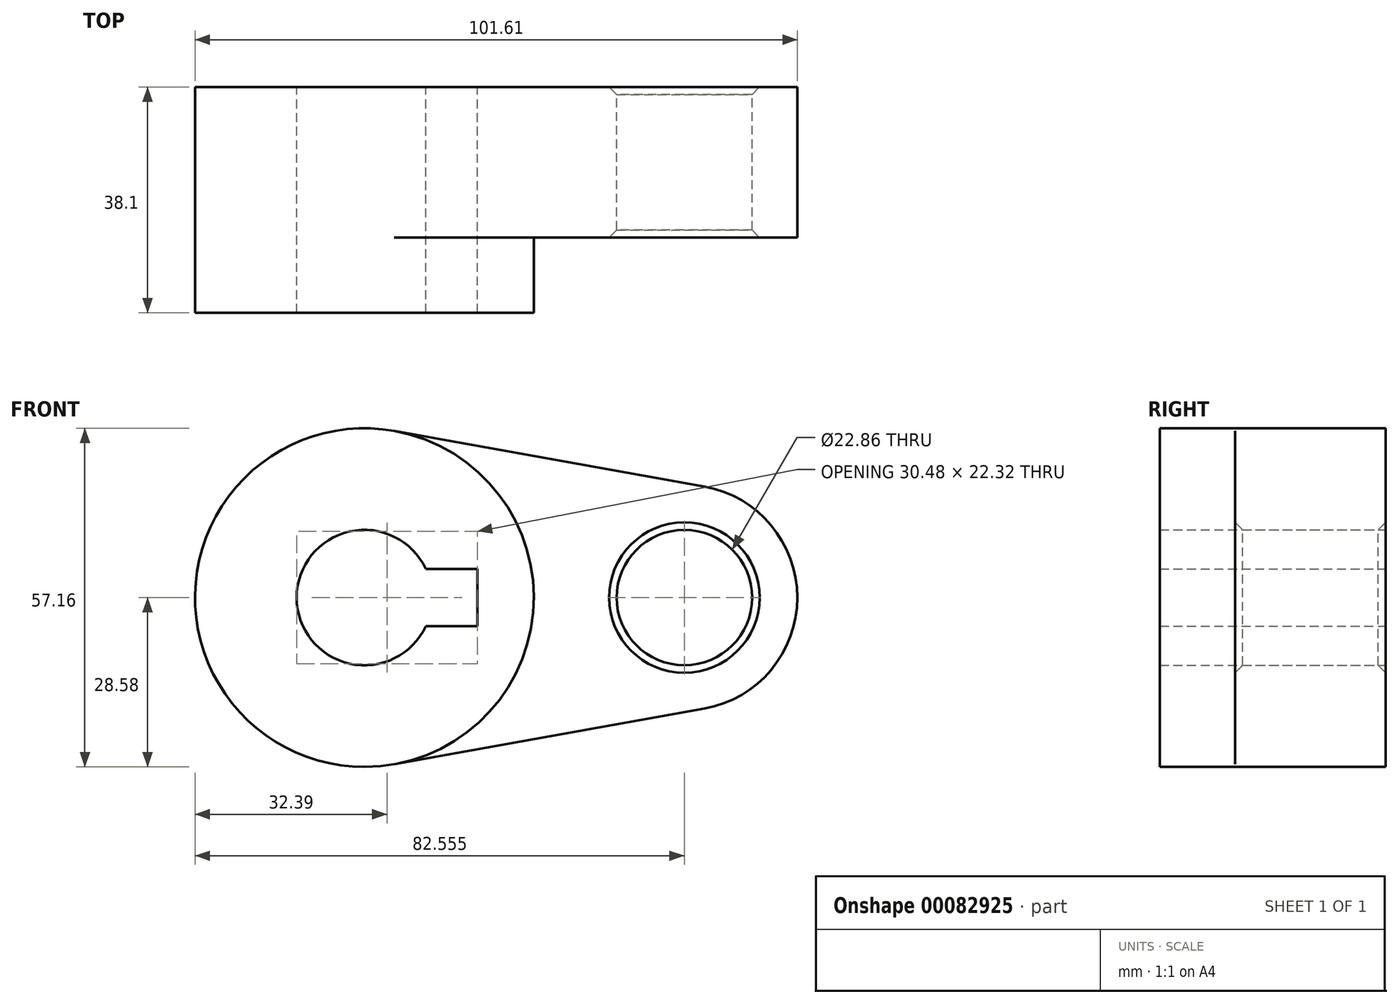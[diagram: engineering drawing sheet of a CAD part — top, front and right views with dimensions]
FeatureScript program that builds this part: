
annotation { "Feature Type Name" : "Feature", "Feature Type Description" : "" }
export const myFeature = defineFeature(function(context is Context, id is Id, definition is map)
    precondition{}
    {
        {
            var Q0;
            Q0=qCreatedBy(makeId("Front.planeOp"),FACE);
            var sketch = newSketch(context, id + "F0", { "sketchPlane" : qUnion([Q0])});
            skCircle(sketch, "E0", {"center": v(0, 0) * mm, "radius": 28.58 * mm});
            skCircle(sketch, "E1", {"center": v(53.98, 0) * mm, "radius": 19.05 * mm});
            skLineSegment(sketch, "E2", {"start": v(5.04, 28.13) * mm, "end": v(57.34, 18.75) * mm});
            skLineSegment(sketch, "E3", {"start": v(57.34, -18.75) * mm, "end": v(5.04, -28.13) * mm});
            skCircle(sketch, "E4", {"center": v(53.98, 0) * mm, "radius": 11.43 * mm});
            skCircle(sketch, "E5", {"center": v(0, 0) * mm, "radius": 11.43 * mm});
            skLineSegment(sketch, "E6.bottom", {"start": v(-19.05, 4.83) * mm, "end": v(19.05, 4.83) * mm});
            skLineSegment(sketch, "E6.top", {"start": v(-19.05, -4.83) * mm, "end": v(19.05, -4.83) * mm});
            skLineSegment(sketch, "E6.left", {"start": v(-19.05, 4.83) * mm, "end": v(-19.05, -4.83) * mm});
            skLineSegment(sketch, "E6.right", {"start": v(19.05, 4.83) * mm, "end": v(19.05, -4.83) * mm});
            skSolve(sketch);
        }
        {
            var Q0;
            {var subQ7=sQuery(id+"F0.wireOp",EDGE,"E6.left");Q0=makeQuery(id+"F0.imprint","IMPRINT",FACE,{"disambiguationData":[TD([[makeQuery(id+"F0.imprint","IMPRINT",EDGE,{"derivedFrom":subQ7}),-1.0]])]});}
            var Q1;
            {var subQ5=sQuery(id+"F0.wireOp",EDGE,"E6.left");Q1=makeQuery(id+"F0.imprint","IMPRINT",FACE,{"disambiguationData":[TD([[makeQuery(id+"F0.imprint","IMPRINT",EDGE,{"derivedFrom":subQ5}),1.0]])]});}
            var Q2;
            {var subQ0=sQuery(id+"F0.wireOp",EDGE,"E2");Q2=makeQuery(id+"F0.imprint","IMPRINT",FACE,{"disambiguationData":[TD([[makeQuery(id+"F0.imprint","IMPRINT",EDGE,{"derivedFrom":subQ0}),-1.0]])]});}
            var Q3;
            Q3=makeQuery(id+"F0.imprint","IMPRINT",FACE,{"disambiguationData":[TD([[makeQuery(id+"F0.imprint","IMPRINT",EDGE,{"derivedFrom":sQuery(id+"F0.wireOp",EDGE,"E4")}),-1.0]])]});
            extrude(context, id + "F1", {"entities" : qUnion([Q0, Q1, Q2, Q3]), "depth" : 25.4 * mm});
        }
        {
            var Q0;
            {var subQ7=sQuery(id+"F0.wireOp",EDGE,"E6.left");Q0=makeQuery(id+"F0.imprint","IMPRINT",FACE,{"disambiguationData":[TD([[makeQuery(id+"F0.imprint","IMPRINT",EDGE,{"derivedFrom":subQ7}),-1.0]])]});}
            var Q1;
            {var subQ5=sQuery(id+"F0.wireOp",EDGE,"E6.left");Q1=makeQuery(id+"F0.imprint","IMPRINT",FACE,{"disambiguationData":[TD([[makeQuery(id+"F0.imprint","IMPRINT",EDGE,{"derivedFrom":subQ5}),1.0]])]});}
            extrude(context, id + "F2", {"entities" : qUnion([Q0, Q1]), "operationType" : NewBodyOperationType.ADD, "depth" : 38.1 * mm});
        }
        {
            var Q0;
            Q0=makeQuery(id+"F1.opExtrude","SWEPT_FACE",FACE,{"disambiguationData":[OSD([sQuery(id+"F0.wireOp",EDGE,"E4")])]});
            chamfer(context, id + "F3", {"entities" : qUnion([Q0]), "width" : 1.27 * mm, "tangentPropagation" : true});
        }
    });
